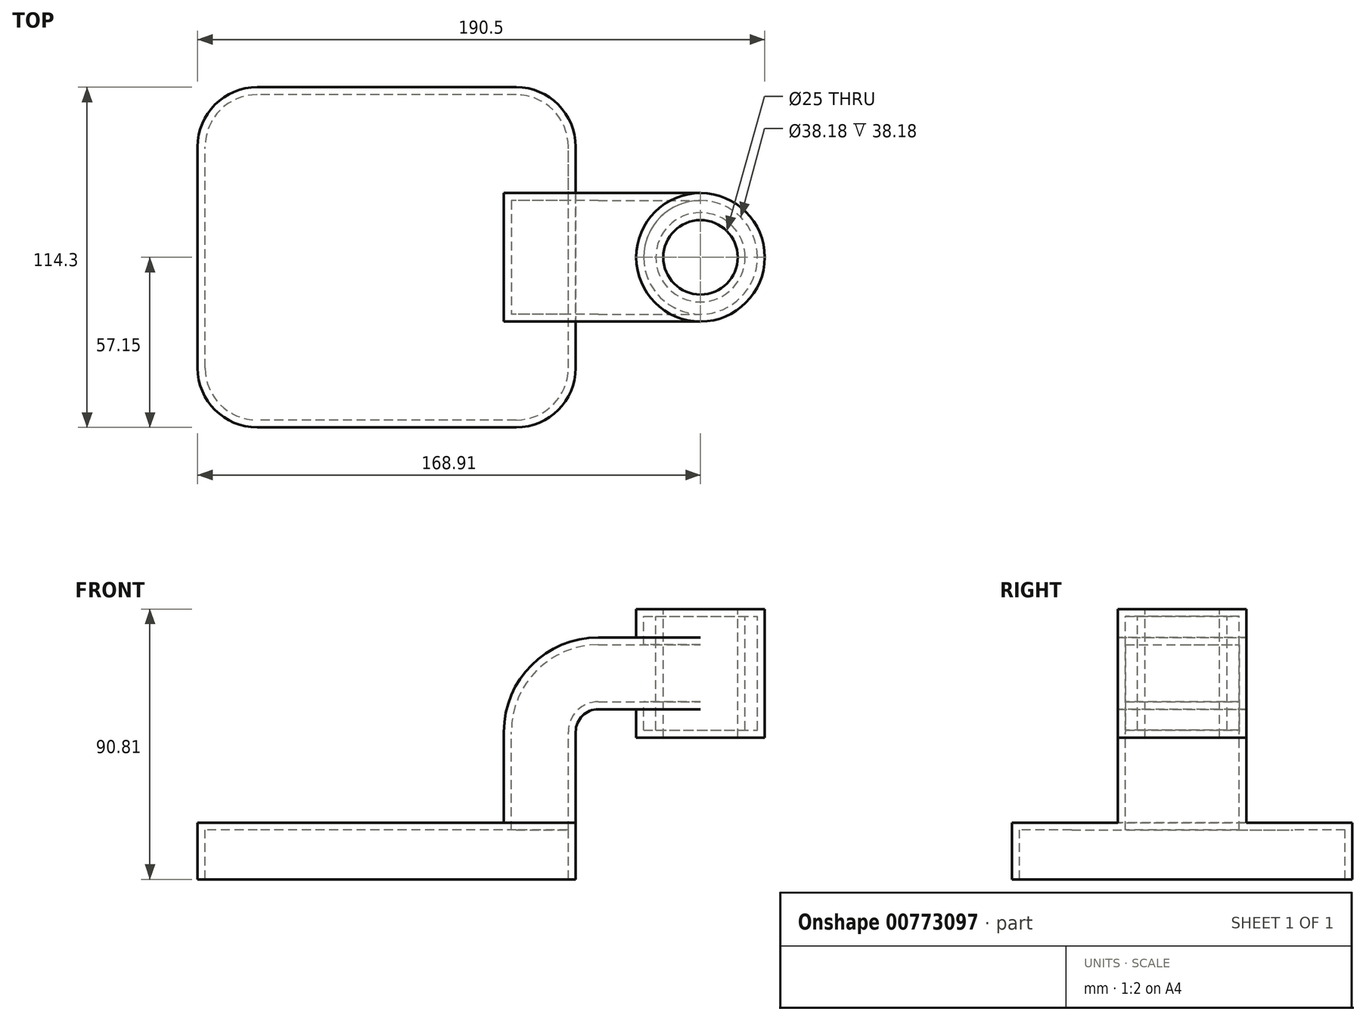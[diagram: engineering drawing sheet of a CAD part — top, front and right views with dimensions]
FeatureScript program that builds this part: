
annotation { "Feature Type Name" : "Feature", "Feature Type Description" : "" }
export const myFeature = defineFeature(function(context is Context, id is Id, definition is map)
    precondition{}
    {
        {
            var Q0;
            Q0=qCreatedBy(makeId("Front.planeOp"),FACE);
            var sketch = newSketch(context, id + "F0", { "sketchPlane" : qUnion([Q0])});
            skLineSegment(sketch, "E0.bottom", {"start": v(63.5, -9.52) * mm, "end": v(-63.5, -9.52) * mm});
            skLineSegment(sketch, "E0.top", {"start": v(63.5, 9.53) * mm, "end": v(-63.5, 9.53) * mm});
            skLineSegment(sketch, "E0.left", {"start": v(63.5, -9.52) * mm, "end": v(63.5, 9.53) * mm});
            skLineSegment(sketch, "E0.right", {"start": v(-63.5, -9.52) * mm, "end": v(-63.5, 9.53) * mm});
            skPoint(sketch, "E0.middle", {"position": v(0, 0) * mm});
            skLineSegment(sketch, "E1.bottom", {"start": v(127, 38.1) * mm, "end": v(83.82, 38.1) * mm});
            skLineSegment(sketch, "E1.top", {"start": v(127, 81.28) * mm, "end": v(83.82, 81.28) * mm});
            skLineSegment(sketch, "E1.left", {"start": v(127, 38.1) * mm, "end": v(127, 81.28) * mm});
            skLineSegment(sketch, "E1.right", {"start": v(83.82, 38.1) * mm, "end": v(83.82, 81.28) * mm});
            skPoint(sketch, "E1.middle", {"position": v(105.41, 59.69) * mm});
            skLineSegment(sketch, "E2", {"start": v(63.5, 9.53) * mm, "end": v(63.5, 40) * mm});
            skArc(sketch, "E3", {"start": v(63.5, 40) * mm, "mid": v(65.73, 45.4) * mm, "end": v(71.12, 47.63) * mm});
            skLineSegment(sketch, "E4", {"start": v(71.12, 47.63) * mm, "end": v(83.82, 47.63) * mm});
            skLineSegment(sketch, "E5.0", {"start": v(71.12, 71.75) * mm, "end": v(83.82, 71.75) * mm});
            skArc(sketch, "E5.1", {"start": v(39.37, 40) * mm, "mid": v(48.67, 62.46) * mm, "end": v(71.12, 71.75) * mm});
            skLineSegment(sketch, "E5.2", {"start": v(39.37, 9.53) * mm, "end": v(39.37, 40) * mm});
            skLineSegment(sketch, "E6", {"start": v(105.4, 81.28) * mm, "end": v(105.41, 38.1) * mm});
            skLineSegment(sketch, "E7", {"start": v(83.82, 71.75) * mm, "end": v(105.41, 71.75) * mm});
            skLineSegment(sketch, "E8", {"start": v(83.82, 47.63) * mm, "end": v(105.41, 47.63) * mm});
            skFitSpline(sketch, "E9", {"points": [v(-63.5, 9.53) * mm, v(-11.4, 57.55) * mm, v(71.12, 71.76) * mm], "startDerivative": vector(0, 138.16) * mm, "endDerivative": vector(220.15, 0) * mm});
            skSolve(sketch);
        }
        {
            var Q0;
            Q0=makeQuery(id+"F0.imprint","IMPRINT",FACE,{"disambiguationData":[TD([[makeQuery(id+"F0.imprint","IMPRINT",EDGE,{"derivedFrom":sQuery(id+"F0.wireOp",EDGE,"E0.bottom")}),-1.0]])]});
            extrude(context, id + "F1", {"entities" : qUnion([Q0]), "depth" : 114.3 * mm, "offsetDistance" : 25.4 * mm, "symmetric" : true});
        }
        {
            var Q0;
            {var subQ0=sQuery(id+"F0.wireOp",EDGE,"E2");Q0=makeQuery(id+"F0.imprint","IMPRINT",FACE,{"disambiguationData":[TD([[makeQuery(id+"F0.imprint","IMPRINT",EDGE,{"derivedFrom":subQ0}),1.0]])]});}
            var Q1;
            {var subQ2=sQuery(id+"F0.wireOp",EDGE,"E7");Q1=makeQuery(id+"F0.imprint","IMPRINT",FACE,{"disambiguationData":[TD([[makeQuery(id+"F0.imprint","IMPRINT",EDGE,{"derivedFrom":subQ2}),-1.0]])]});}
            extrude(context, id + "F2", {"entities" : qUnion([Q0, Q1]), "operationType" : NewBodyOperationType.ADD, "oppositeDirection" : true, "depth" : (1.7 * 25.4) * mm, "offsetDistance" : 25.4 * mm, "symmetric" : true});
        }
        {
            var Q0;
            Q0=makeQuery(id+"F0.imprint","IMPRINT",FACE,{"disambiguationData":[TD([[makeQuery(id+"F0.imprint","IMPRINT",EDGE,{"derivedFrom":sQuery(id+"F0.wireOp",EDGE,"E5.1")}),1.0]])]});
            extrude(context, id + "F3", {"entities" : qUnion([Q0]), "operationType" : NewBodyOperationType.ADD, "oppositeDirection" : true, "depth" : 25 * mm, "offsetDistance" : 25 * mm, "symmetric" : true});
        }
        {
            var Q0;
            {var subQ4=sQuery(id+"F0.wireOp",EDGE,"E1.left");Q0=makeQuery(id+"F0.imprint","IMPRINT",FACE,{"disambiguationData":[TD([[makeQuery(id+"F0.imprint","IMPRINT",EDGE,{"derivedFrom":subQ4}),1.0]])]});}
            var Q1;
            Q1=sQuery(id+"F0.wireOp",EDGE,"E6");
            revolve(context, id + "F4", {"operationType" : NewBodyOperationType.ADD, "surfaceOperationType" : NewSurfaceOperationType.NEW, "entities" : qUnion([Q0]), "axis" : qUnion([Q1]), "revolveType" : RevolveType.FULL});
        }
        {
            var Q0;
            Q0=makeQuery(id+"F4.opRevolve","SWEPT_FACE",FACE,{"disambiguationData":[OSD([sQuery(id+"F0.wireOp",EDGE,"E1.top")])]});
            var sketch = newSketch(context, id + "F5", { "sketchPlane" : qUnion([Q0])});
            skCircle(sketch, "E10", {"center": v(105.41, 0) * mm, "radius": 12.5 * mm});
            skSolve(sketch);
        }
        {
            var Q0;
            Q0=makeQuery(id+"F5.imprint","IMPRINT",FACE,{"disambiguationData":[TD([[makeQuery(id+"F5.imprint","IMPRINT",EDGE,{"derivedFrom":sQuery(id+"F5.wireOp",EDGE,"E10")}),1.0]])]});
            extrude(context, id + "F6", {"entities" : qUnion([Q0]), "operationType" : NewBodyOperationType.REMOVE, "endBound" : BoundingType.THROUGH_ALL, "oppositeDirection" : true, "depth" : 25 * mm, "offsetDistance" : 25 * mm});
        }
        {
            var Q0;
            Q0=makeQuery(id+"F1.opExtrude","CAP_EDGE",EDGE,{"disambiguationData":[OSD([sQuery(id+"F0.wireOp",EDGE,"E0.left")])],"isStart":false});
            var Q1;
            Q1=makeQuery(id+"F1.opExtrude","CAP_EDGE",EDGE,{"disambiguationData":[OSD([sQuery(id+"F0.wireOp",EDGE,"E0.right")])],"isStart":false});
            var Q2;
            Q2=makeQuery(id+"F1.opExtrude","CAP_EDGE",EDGE,{"disambiguationData":[OSD([sQuery(id+"F0.wireOp",EDGE,"E0.left")])],"isStart":true});
            var Q3;
            Q3=makeQuery(id+"F1.opExtrude","CAP_EDGE",EDGE,{"disambiguationData":[OSD([sQuery(id+"F0.wireOp",EDGE,"E0.right")])],"isStart":true});
            fillet(context, id + "F7", {"entities" : qUnion([Q0, Q1, Q2, Q3]), "radius" : 20 * mm, "tangentPropagation" : true, "allowEdgeOverflow" : false});
        }
        {
            var Q0;
            Q0=makeQuery(id+"F1.opExtrude","SWEPT_FACE",FACE,{"disambiguationData":[OSD([sQuery(id+"F0.wireOp",EDGE,"E0.bottom")])]});
            shell(context, id + "F8", {"entities" : qUnion([Q0]), "thickness" : 2.5 * mm});
        }
    });
